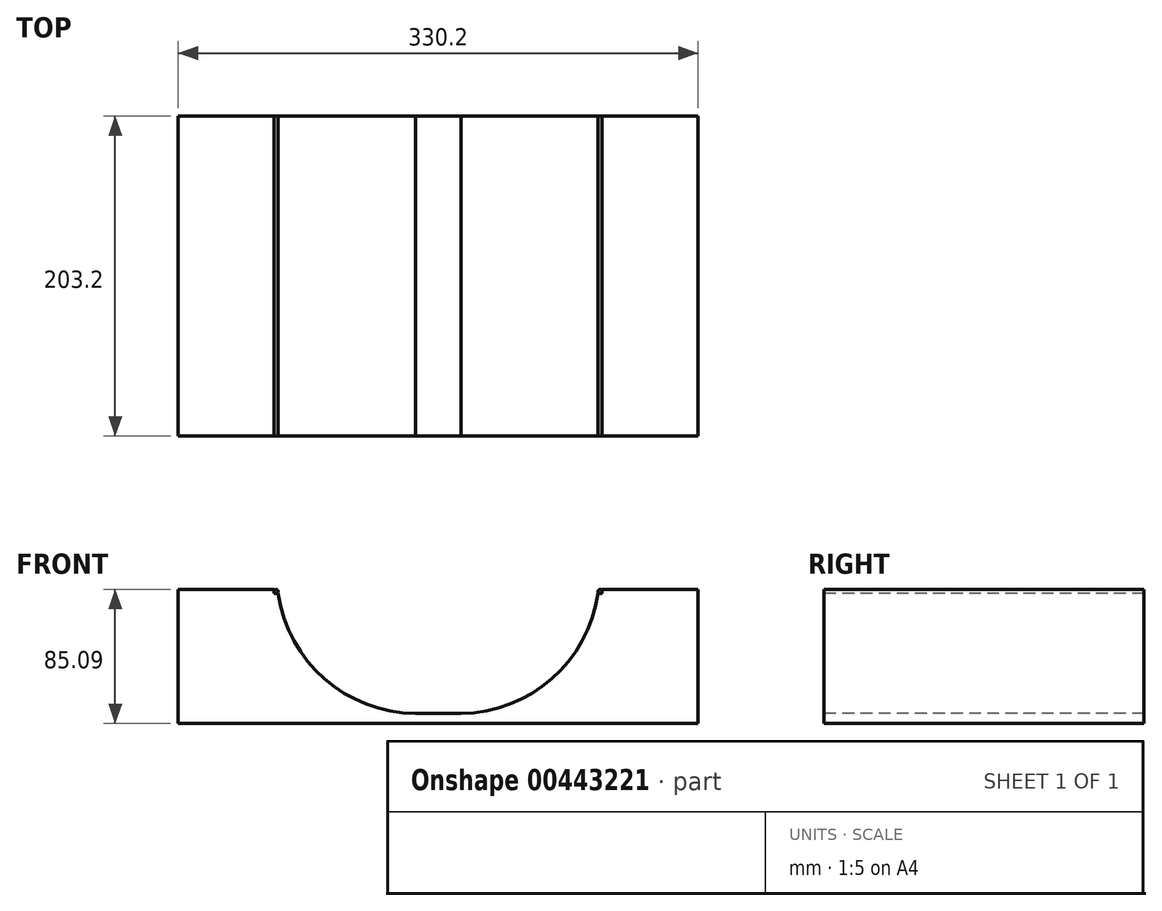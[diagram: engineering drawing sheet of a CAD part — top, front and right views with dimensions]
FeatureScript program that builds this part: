
annotation { "Feature Type Name" : "Feature", "Feature Type Description" : "" }
export const myFeature = defineFeature(function(context is Context, id is Id, definition is map)
    precondition{}
    {
        {
            var Q0;
            Q0=qCreatedBy(makeId("Front.planeOp"),FACE);
            var sketch = newSketch(context, id + "F0", { "sketchPlane" : qUnion([Q0])});
            skLineSegment(sketch, "E0.bottom", {"start": v(0, 0) * mm, "end": v(203.2, 0) * mm});
            skLineSegment(sketch, "E0.top", {"start": v(0, 6.35) * mm, "end": v(203.2, 6.35) * mm});
            skLineSegment(sketch, "E0.left", {"start": v(0, 0) * mm, "end": v(0, 6.35) * mm});
            skLineSegment(sketch, "E0.right", {"start": v(203.2, 0) * mm, "end": v(203.2, 6.35) * mm});
            skSolve(sketch);
        }
        {
            var Q0;
            Q0 = qSketchRegion(id + "F0", true);
            extrude(context, id + "F1", {"entities" : qUnion([Q0]), "endBound" : BoundingType.SYMMETRIC, "depth" : 203.2 * mm});
        }
        {
            var Q0;
            Q0=makeQuery(id+"F1.opExtrude","CAP_FACE",FACE,{"disambiguationData":[OSD([sQuery(id+"F0.wireOp",EDGE,"E0.bottom"),sQuery(id+"F0.wireOp",EDGE,"E0.top"),sQuery(id+"F0.wireOp",EDGE,"E0.left"),sQuery(id+"F0.wireOp",EDGE,"E0.right")])],"isStart":false});
            var sketch = newSketch(context, id + "F2", { "sketchPlane" : qUnion([Q0])});
            skLineSegment(sketch, "E1", {"start": v(101.6, 6.35) * mm, "end": v(101.6, 111.26) * mm, "construction": true});
            skPoint(sketch, "E1.endSnap0", {"position": v(101.6, 6.35) * mm});
            skArc(sketch, "E2", {"start": v(0, 82.55) * mm, "mid": v(30.13, 27.75) * mm, "end": v(88.9, 6.35) * mm});
            skLineSegment(sketch, "E3", {"start": v(0, 6.35) * mm, "end": v(0, 82.55) * mm});
            skArc(sketch, "E4", {"start": v(114.3, 6.35) * mm, "mid": v(173.07, 27.75) * mm, "end": v(203.2, 82.55) * mm});
            skLineSegment(sketch, "E5", {"start": v(203.2, 6.35) * mm, "end": v(203.2, 82.55) * mm});
            skLineSegment(sketch, "E6", {"start": v(0, 6.35) * mm, "end": v(88.9, 6.35) * mm});
            skLineSegment(sketch, "E7", {"start": v(114.3, 6.35) * mm, "end": v(203.2, 6.35) * mm});
            skLineSegment(sketch, "E8.bottom", {"start": v(0, 0) * mm, "end": v(-63.5, 0) * mm});
            skLineSegment(sketch, "E8.top", {"start": v(0, 82.55) * mm, "end": v(-63.5, 82.55) * mm});
            skLineSegment(sketch, "E8.left", {"start": v(0, 0) * mm, "end": v(0, 82.55) * mm});
            skLineSegment(sketch, "E8.right", {"start": v(-63.5, 0) * mm, "end": v(-63.5, 82.55) * mm});
            skLineSegment(sketch, "E9.bottom", {"start": v(203.2, 0) * mm, "end": v(266.7, 0) * mm});
            skLineSegment(sketch, "E9.top", {"start": v(203.2, 82.55) * mm, "end": v(266.7, 82.55) * mm});
            skLineSegment(sketch, "E9.left", {"start": v(203.2, 0) * mm, "end": v(203.2, 82.55) * mm});
            skLineSegment(sketch, "E9.right", {"start": v(266.7, 0) * mm, "end": v(266.7, 82.55) * mm});
            skSolve(sketch);
        }
        {
            var Q0;
            {var subQ1=sQuery(id+"F2.wireOp",EDGE,"E8.bottom");Q0=makeQuery(id+"F2.imprint","IMPRINT",FACE,{"disambiguationData":[TD([[makeQuery(id+"F2.imprint","IMPRINT",EDGE,{"derivedFrom":subQ1}),-1.0]])]});}
            var Q1;
            {var subQ0=sQuery(id+"F2.wireOp",EDGE,"E8.left");var subQ3=sQuery(id+"F2.wireOp",EDGE,"E6");var subQ5=makeQuery(id+"F2.imprint","INTERSECT",VERTEX,{"derivedFrom":[subQ3,subQ0]});Q1=makeQuery(id+"F2.imprint","IMPRINT",FACE,{"disambiguationData":[TD([[makeQuery(id+"F2.imprint","IMPRINT",EDGE,{"disambiguationData":[TD([[subQ5,-1.0]])],"derivedFrom":subQ3}),1.0]])]});}
            var Q2;
            {var subQ0=sQuery(id+"F2.wireOp",EDGE,"E9.left");var subQ3=sQuery(id+"F2.wireOp",EDGE,"E7");var subQ5=makeQuery(id+"F2.imprint","INTERSECT",VERTEX,{"derivedFrom":[subQ3,subQ0]});Q2=makeQuery(id+"F2.imprint","IMPRINT",FACE,{"disambiguationData":[TD([[makeQuery(id+"F2.imprint","IMPRINT",EDGE,{"disambiguationData":[TD([[subQ5,1.0]])],"derivedFrom":subQ3}),1.0]])]});}
            var Q3;
            {var subQ1=sQuery(id+"F2.wireOp",EDGE,"E9.bottom");Q3=makeQuery(id+"F2.imprint","IMPRINT",FACE,{"disambiguationData":[TD([[makeQuery(id+"F2.imprint","IMPRINT",EDGE,{"derivedFrom":subQ1}),1.0]])]});}
            extrude(context, id + "F3", {"entities" : qUnion([Q0, Q1, Q2, Q3]), "operationType" : NewBodyOperationType.ADD, "oppositeDirection" : true, "depth" : 203.2 * mm});
        }
        {
            var Q0;
            Q0=makeQuery(id+"F3.boolean.opBoolean","MERGE",FACE,{"derivedFrom":[makeQuery(id+"F1.opExtrude","CAP_FACE",FACE,{"disambiguationData":[OSD([sQuery(id+"F0.wireOp",EDGE,"E0.bottom"),sQuery(id+"F0.wireOp",EDGE,"E0.top"),sQuery(id+"F0.wireOp",EDGE,"E0.left"),sQuery(id+"F0.wireOp",EDGE,"E0.right")])],"isStart":false}),makeQuery(id+"F3.opExtrude","CAP_FACE",FACE,{"disambiguationData":[OSD([sQuery(id+"F2.wireOp",EDGE,"E2"),sQuery(id+"F2.wireOp",EDGE,"E6"),sQuery(id+"F2.wireOp",EDGE,"E8.bottom"),sQuery(id+"F2.wireOp",EDGE,"E8.top"),sQuery(id+"F2.wireOp",EDGE,"E8.left"),sQuery(id+"F2.wireOp",EDGE,"E8.right")])],"isStart":true}),makeQuery(id+"F3.opExtrude","CAP_FACE",FACE,{"disambiguationData":[OSD([sQuery(id+"F2.wireOp",EDGE,"E4"),sQuery(id+"F2.wireOp",EDGE,"E7"),sQuery(id+"F2.wireOp",EDGE,"E9.bottom"),sQuery(id+"F2.wireOp",EDGE,"E9.top"),sQuery(id+"F2.wireOp",EDGE,"E9.left"),sQuery(id+"F2.wireOp",EDGE,"E9.right")])],"isStart":true})]});
            var sketch = newSketch(context, id + "F4", { "sketchPlane" : qUnion([Q0])});
            skCircle(sketch, "E10", {"center": v(204.47, 83.82) * mm, "radius": 1.27 * mm});
            skCircle(sketch, "E11", {"center": v(-1.27, 83.82) * mm, "radius": 1.27 * mm});
            skSolve(sketch);
        }
        {
            var Q0;
            Q0=makeQuery(id+"F4.imprint","IMPRINT",FACE,{"disambiguationData":[TD([[makeQuery(id+"F4.imprint","IMPRINT",EDGE,{"derivedFrom":sQuery(id+"F4.wireOp",EDGE,"E11")}),1.0]])]});
            var Q1;
            Q1=makeQuery(id+"F4.imprint","IMPRINT",FACE,{"disambiguationData":[TD([[makeQuery(id+"F4.imprint","IMPRINT",EDGE,{"derivedFrom":sQuery(id+"F4.wireOp",EDGE,"E10")}),1.0]])]});
            extrude(context, id + "F5", {"entities" : qUnion([Q0, Q1]), "oppositeDirection" : true, "depth" : 203.2 * mm});
        }
        {
            var Q0;
            Q0=makeQuery(id+"F3.boolean.opBoolean","MERGE",FACE,{"derivedFrom":[makeQuery(id+"F1.opExtrude","CAP_FACE",FACE,{"disambiguationData":[OSD([sQuery(id+"F0.wireOp",EDGE,"E0.bottom"),sQuery(id+"F0.wireOp",EDGE,"E0.top"),sQuery(id+"F0.wireOp",EDGE,"E0.left"),sQuery(id+"F0.wireOp",EDGE,"E0.right")])],"isStart":false}),makeQuery(id+"F3.opExtrude","CAP_FACE",FACE,{"disambiguationData":[OSD([sQuery(id+"F2.wireOp",EDGE,"E2"),sQuery(id+"F2.wireOp",EDGE,"E6"),sQuery(id+"F2.wireOp",EDGE,"E8.bottom"),sQuery(id+"F2.wireOp",EDGE,"E8.top"),sQuery(id+"F2.wireOp",EDGE,"E8.left"),sQuery(id+"F2.wireOp",EDGE,"E8.right")])],"isStart":true}),makeQuery(id+"F3.opExtrude","CAP_FACE",FACE,{"disambiguationData":[OSD([sQuery(id+"F2.wireOp",EDGE,"E4"),sQuery(id+"F2.wireOp",EDGE,"E7"),sQuery(id+"F2.wireOp",EDGE,"E9.bottom"),sQuery(id+"F2.wireOp",EDGE,"E9.top"),sQuery(id+"F2.wireOp",EDGE,"E9.left"),sQuery(id+"F2.wireOp",EDGE,"E9.right")])],"isStart":true})]});
            var sketch = newSketch(context, id + "F6", { "sketchPlane" : qUnion([Q0])});
            skLineSegment(sketch, "E12.bottom", {"start": v(-63.5, 82.55) * mm, "end": v(-2.54, 82.55) * mm});
            skLineSegment(sketch, "E12.top", {"start": v(-63.5, 85.1) * mm, "end": v(-2.54, 85.1) * mm});
            skLineSegment(sketch, "E12.left", {"start": v(-63.5, 82.55) * mm, "end": v(-63.5, 85.1) * mm});
            skLineSegment(sketch, "E12.right", {"start": v(-2.54, 82.55) * mm, "end": v(-2.54, 85.1) * mm});
            skLineSegment(sketch, "E13.bottom", {"start": v(266.7, 82.55) * mm, "end": v(205.74, 82.55) * mm});
            skLineSegment(sketch, "E13.top", {"start": v(266.7, 85.1) * mm, "end": v(205.74, 85.1) * mm});
            skLineSegment(sketch, "E13.left", {"start": v(266.7, 82.55) * mm, "end": v(266.7, 85.1) * mm});
            skLineSegment(sketch, "E13.right", {"start": v(205.74, 82.55) * mm, "end": v(205.74, 85.1) * mm});
            skSolve(sketch);
        }
        {
            var Q0;
            Q0 = qSketchRegion(id + "F6", true);
            extrude(context, id + "F7", {"entities" : qUnion([Q0]), "oppositeDirection" : true, "depth" : 203.2 * mm});
        }
        {
            var Q0;
            Q0=makeQuery(id+"F1.opExtrude","SWEPT_BODY",BODY,{"disambiguationData":[OSD([sQuery(id+"F0.wireOp",EDGE,"E0.bottom"),sQuery(id+"F0.wireOp",EDGE,"E0.top"),sQuery(id+"F0.wireOp",EDGE,"E0.left"),sQuery(id+"F0.wireOp",EDGE,"E0.right")])]});
            var Q1;
            Q1=makeQuery(id+"F5.opExtrude","SWEPT_BODY",BODY,{"disambiguationData":[OSD([sQuery(id+"F4.wireOp",EDGE,"E11")])]});
            var Q2;
            Q2=makeQuery(id+"F5.opExtrude","SWEPT_BODY",BODY,{"disambiguationData":[OSD([sQuery(id+"F4.wireOp",EDGE,"E10")])]});
            var Q3;
            Q3=makeQuery(id+"F7.opExtrude","SWEPT_BODY",BODY,{"disambiguationData":[OSD([sQuery(id+"F6.wireOp",EDGE,"E12.bottom"),sQuery(id+"F6.wireOp",EDGE,"E12.top"),sQuery(id+"F6.wireOp",EDGE,"E12.left"),sQuery(id+"F6.wireOp",EDGE,"E12.right")])]});
            var Q4;
            Q4=makeQuery(id+"F7.opExtrude","SWEPT_BODY",BODY,{"disambiguationData":[OSD([sQuery(id+"F6.wireOp",EDGE,"E13.bottom"),sQuery(id+"F6.wireOp",EDGE,"E13.top"),sQuery(id+"F6.wireOp",EDGE,"E13.left"),sQuery(id+"F6.wireOp",EDGE,"E13.right")])]});
            booleanBodies(context, id + "F8", {"operationType" : BooleanOperationType.UNION, "tools" : qUnion([Q0, Q1, Q2, Q3, Q4])});
        }
    });
